# Revit family: Flush_Valve_Urinal-Exposed-American_Standard-Selectronic-606X_Series
name_source: partatom
category: Plumbing Fixtures
revit_build: Autodesk Revit 2014 (Build: 20130308_1515(x64)
units: mm (PartAtom-declared; Revit-internal decimal feet)

## types (9) — shared parameters
ADA Compliant = Yes
Assembly Code = D2020100
CW Connection = Yes
CWFU = 5
Cold Water Connection Diameter = 3/4"
Cold Water Connection Height = 11 1/2"
Cold Water Connection Radius = 3/8"
Cold Water Connection Width = 4 3/4"
Default Elevation = 0"
HW Connection = No
Height = 16 1/2"
Installation Type = Exposed
Length = 2 1/4"
Manufacturer = American Standard
Material = Metal-American Standard-002-Polished Chrome
Price = Prices may vary. Please consult Manufacturer Representative for most up-to-date price list.
Revised Date = 12/23/2016
URL = http://www.americanstandard-us.com
Vent Connection = No
Warranty Information = 1 Year Limited Warranty
Waste Connection = No
Width = 2 7/8"
zero-valued in all types: HWFU, WFU

## per-type parameters (varying)
| type | Battery Life | Description | Flush Rate | Model | Product Documentation Link | Product Page URL |
| 6063.025 | 4 years @ 4,000 cycles per month (192,000 cycles) | Selectronic Sensor-Operated Urinal Flush Valve, 0.25 GPF Battery Powered. | 0.25 Gpf (1.0Lpf) | 6063.025.002 | https://www.americanstandard-us.com | https://www.americanstandard-us.com |
| 6063.051 | 4 years @ 4,000 cycles per month | Selectronic Sensor-Operated Urinal Flush Valve, 0.5 GPF Battery Powered. | 0.5 Gpf (1.9 Lpf) | 6063.051.002 | https://www.americanstandard-us.com | https://www.americanstandard-us.com |
| 6063.013 | 4 years @ 4,000 cycles per month (192,000 cycles) | Selectronic Sensor-Operated Urinal Flush Valve, 0.125 GPF Battery Powered. | 0.125 Gpf (0.5 Lpf) | 6063.013.002 | https://www.americanstandard-us.com | https://www.americanstandard-us.com |
| 6063.101 | 4 years @ 4,000 cycles per month (192,000 cycles). | Selectronic Sensor-Operated Urinal Flush Valve, 1.0 GPF Battery Powered. | 1.0 Gpf (3.8 Lpf) | 6063.101.002 | http://www.americanstandard-us.com | http://www.americanstandard-us.com |
| 6064.101 | 10 years @ 4,000 cycles per month. | Selectronic Sensor-Operated Urinal Flush Valve, 1.0 GPF PWRX Battery Powered. | 1.0 Gpf (3.8 Lpf) | 6064.101.002 | https://www.americanstandard-us.com | https://www.americanstandard-us.com |
| 6064.051 | 10 years @ 4,000 cycles per month | Selectronic Sensor-Operated Urinal Flush Valve, 0.5 GPF PWRX Battery Powered. | 0.5 Gpf (1.9 Lpf) | 6064.051.002 | https://www.americanstandard-us.com | https://www.americanstandard-us.com |
| 6064.025 | 10 years @ 4,000 cycles per month. | Selectronic Sensor-Operated Urinal Flush Valve, 0.25 GPF PWX Battery Powered. | 0.25 Gpf (1.0Lpf) | 6064.025.002 | https://www.americanstandard-us.com | https://www.americanstandard-us.com |
| 6064.513 | 10 years @ 4,000 cycles per month. | Selectronic Sensor-Operated Urinal Flush Valve, 0.125 GPF PWRX Battery Powered. | 0.125 Gpf (0.5 Lpf) | 6064.513.002 | http://www.americanstandard-us.com | http://www.americanstandard-us.com |
| 6064.013 | 10 years @ 4,000 cycles per month. | Selectronic Sensor-Operated Urinal Flush Valve, 0.125 GPF PWX Battery Powered. | 0.125 Gpf (0.5Lpf) | 6064.013.002 | https://www.americanstandard-us.com | https://www.americanstandard-us.com |

## geometry (parser evidence)
native form markers: Sweep x2
no freeform markers — native parametric forms only
